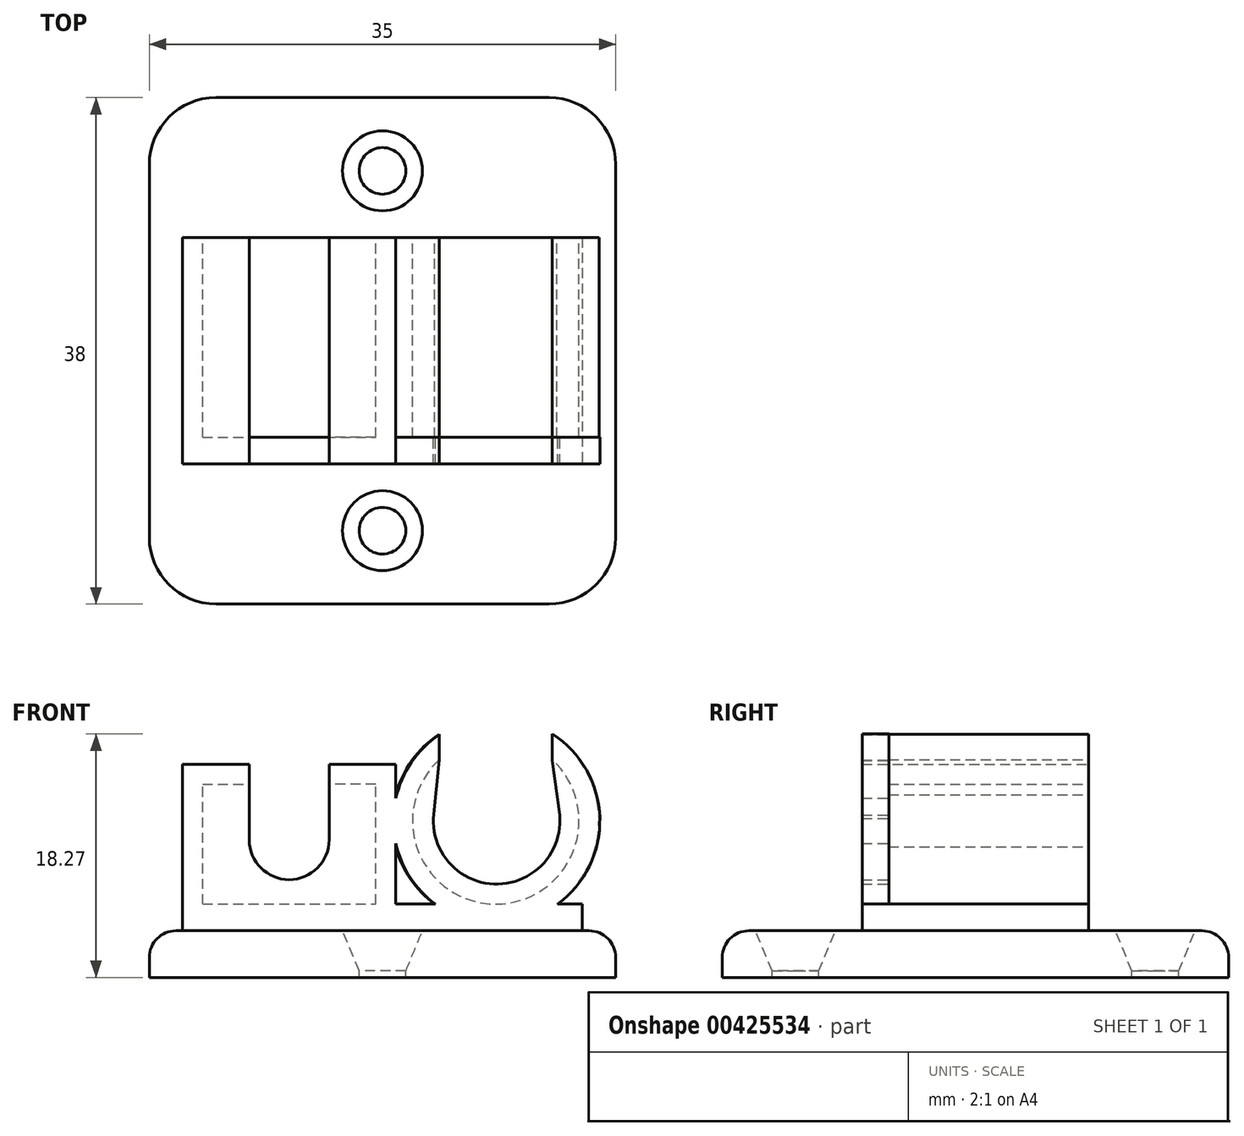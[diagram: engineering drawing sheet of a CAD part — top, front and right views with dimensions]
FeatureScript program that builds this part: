
annotation { "Feature Type Name" : "Feature", "Feature Type Description" : "" }
export const myFeature = defineFeature(function(context is Context, id is Id, definition is map)
    precondition{}
    {
        {
            var Q0;
            Q0=qCreatedBy(makeId("Top.planeOp"),FACE);
            var sketch = newSketch(context, id + "F0", { "sketchPlane" : qUnion([Q0])});
            skLineSegment(sketch, "E0.bottom", {"start": v(-17.5, 19) * mm, "end": v(17.5, 19) * mm});
            skLineSegment(sketch, "E0.top", {"start": v(-17.5, -19) * mm, "end": v(17.5, -19) * mm});
            skLineSegment(sketch, "E0.left", {"start": v(-17.5, 19) * mm, "end": v(-17.5, -19) * mm});
            skLineSegment(sketch, "E0.right", {"start": v(17.5, 19) * mm, "end": v(17.5, -19) * mm});
            skSolve(sketch);
        }
        {
            var Q0;
            Q0 = qSketchRegion(id + "F0", true);
            extrude(context, id + "F1", {"entities" : qUnion([Q0]), "depth" : 3.5 * mm});
        }
        {
            var Q0;
            Q0=makeQuery(id+"F1.opExtrude","CAP_FACE",FACE,{"disambiguationData":[OSD([sQuery(id+"F0.wireOp",EDGE,"E0.bottom"),sQuery(id+"F0.wireOp",EDGE,"E0.top"),sQuery(id+"F0.wireOp",EDGE,"E0.left"),sQuery(id+"F0.wireOp",EDGE,"E0.right")])],"isStart":false});
            var sketch = newSketch(context, id + "F2", { "sketchPlane" : qUnion([Q0])});
            skLineSegment(sketch, "E1.bottom", {"start": v(-15, 8.5) * mm, "end": v(15, 8.5) * mm});
            skLineSegment(sketch, "E1.top", {"start": v(-15, -8.5) * mm, "end": v(15, -8.5) * mm});
            skLineSegment(sketch, "E1.left", {"start": v(-15, 8.5) * mm, "end": v(-15, -8.5) * mm});
            skLineSegment(sketch, "E1.right", {"start": v(15, 8.5) * mm, "end": v(15, -8.5) * mm});
            skSolve(sketch);
        }
        {
            var Q0;
            Q0 = qSketchRegion(id + "F2", true);
            extrude(context, id + "F3", {"entities" : qUnion([Q0]), "operationType" : NewBodyOperationType.ADD, "depth" : 2 * mm});
        }
        {
            var Q0;
            Q0=makeQuery(id+"F3.opExtrude","SWEPT_FACE",FACE,{"disambiguationData":[OSD([sQuery(id+"F2.wireOp",EDGE,"E1.bottom")])]});
            var sketch = newSketch(context, id + "F4", { "sketchPlane" : qUnion([Q0])});
            skLineSegment(sketch, "E2.0", {"start": v(-12.75, 16.33) * mm, "end": v(-12.75, 18.23) * mm});
            skLineSegment(sketch, "E3.0", {"start": v(-4.25, 16.33) * mm, "end": v(-4.25, 18.23) * mm});
            skArc(sketch, "E4", {"start": v(-12.75, 16.33) * mm, "mid": v(-8.5, 5.5) * mm, "end": v(-4.25, 16.33) * mm});
            skArc(sketch, "E5", {"start": v(-12.75, 18.23) * mm, "mid": v(-8.5, 4) * mm, "end": v(-4.25, 18.23) * mm});
            skLineSegment(sketch, "E6", {"start": v(15, 5.5) * mm, "end": v(15, 16) * mm});
            skLineSegment(sketch, "E7.0", {"start": v(-1, 5.5) * mm, "end": v(-1, 16) * mm});
            skLineSegment(sketch, "E8", {"start": v(15, 16) * mm, "end": v(10, 16) * mm});
            skLineSegment(sketch, "E9", {"start": v(10, 16) * mm, "end": v(10, 14.5) * mm});
            skLineSegment(sketch, "E10", {"start": v(-1, 16) * mm, "end": v(4, 16) * mm});
            skLineSegment(sketch, "E11", {"start": v(4, 16) * mm, "end": v(4, 14.5) * mm});
            skLineSegment(sketch, "E12.0", {"start": v(13.5, 5.5) * mm, "end": v(13.5, 14.5) * mm});
            skLineSegment(sketch, "E13.0", {"start": v(0.5, 5.5) * mm, "end": v(0.5, 14.5) * mm});
            skLineSegment(sketch, "E14.0", {"start": v(0.5, 14.5) * mm, "end": v(4, 14.5) * mm});
            skLineSegment(sketch, "E15.0", {"start": v(13.5, 14.5) * mm, "end": v(10, 14.5) * mm});
            skLineSegment(sketch, "E16", {"start": v(-1, 5.5) * mm, "end": v(0.5, 5.5) * mm});
            skLineSegment(sketch, "E17", {"start": v(13.5, 5.5) * mm, "end": v(15, 5.5) * mm});
            skSolve(sketch);
        }
        {
            var Q0;
            Q0 = qSketchRegion(id + "F4", true);
            extrude(context, id + "F5", {"entities" : qUnion([Q0]), "operationType" : NewBodyOperationType.ADD, "oppositeDirection" : true, "depth" : 15 * mm});
        }
        {
            var Q0;
            Q0=makeQuery(id+"F1.opExtrude","CAP_FACE",FACE,{"disambiguationData":[OSD([sQuery(id+"F0.wireOp",EDGE,"E0.bottom"),sQuery(id+"F0.wireOp",EDGE,"E0.top"),sQuery(id+"F0.wireOp",EDGE,"E0.left"),sQuery(id+"F0.wireOp",EDGE,"E0.right")])],"isStart":false});
            var sketch = newSketch(context, id + "F6", { "sketchPlane" : qUnion([Q0])});
            skPoint(sketch, "E18", {"position": v(0, 13.5) * mm});
            skPoint(sketch, "E19", {"position": v(0, -13.5) * mm});
            skPoint(sketch, "E19.positionSnap0", {"position": v(0, 8.5) * mm});
            skSolve(sketch);
        }
        {
            var Q0;
            Q0=sQuery(id+"F6.wireOp",VERTEX,"E18");
            var Q1;
            Q1=sQuery(id+"F6.wireOp",VERTEX,"E19");
            var Q2;
            Q2=makeQuery(id+"F1.opExtrude","SWEPT_BODY",BODY,{"disambiguationData":[OSD([sQuery(id+"F0.wireOp",EDGE,"E0.bottom"),sQuery(id+"F0.wireOp",EDGE,"E0.top"),sQuery(id+"F0.wireOp",EDGE,"E0.left"),sQuery(id+"F0.wireOp",EDGE,"E0.right")])]});
            hole(context, id + "F7", {"style" : HoleStyle.C_SINK, "endStyle" : HoleEndStyle.BLIND, "holeDiameter" : 3.5 * mm, "cSinkDiameter" : 6 * mm, "cSinkAngle" : 45 * degree, "holeDepth" : 10 * mm, "isTappedThrough" : true, "tappedDepth" : 12 * mm, "tapClearance" : 3, "startFromSketch" : true, "locations" : qUnion([Q0, Q1]), "scope" : qUnion([Q2])});
        }
        {
            var Q0;
            Q0=makeQuery(id+"F5.opExtrude","CAP_FACE",FACE,{"disambiguationData":[OSD([sQuery(id+"F4.wireOp",EDGE,"E6"),sQuery(id+"F4.wireOp",EDGE,"E8"),sQuery(id+"F4.wireOp",EDGE,"E9"),sQuery(id+"F4.wireOp",EDGE,"E12.0"),sQuery(id+"F4.wireOp",EDGE,"E15.0"),sQuery(id+"F4.wireOp",EDGE,"E17")])],"isStart":false});
            var sketch = newSketch(context, id + "F8", { "sketchPlane" : qUnion([Q0])});
            skLineSegment(sketch, "E20.bottom", {"start": v(-15, 16) * mm, "end": v(-10, 16) * mm});
            skLineSegment(sketch, "E20.top", {"start": v(-15, 5.45) * mm, "end": v(1, 5.45) * mm});
            skLineSegment(sketch, "E20.left", {"start": v(-15, 16) * mm, "end": v(-15, 5.45) * mm});
            skLineSegment(sketch, "E20.right", {"start": v(1, 16) * mm, "end": v(1, 5.45) * mm});
            skLineSegment(sketch, "E21", {"start": v(-10, 16) * mm, "end": v(-10, 10.33) * mm});
            skLineSegment(sketch, "E22", {"start": v(-4, 16) * mm, "end": v(-4, 10.33) * mm});
            skLineSegment(sketch, "E23", {"start": v(-10, 10.33) * mm, "end": v(-10, 10.33) * mm});
            skArc(sketch, "E24", {"start": v(-10, 10.33) * mm, "mid": v(-7, 7.33) * mm, "end": v(-4, 10.33) * mm});
            skLineSegment(sketch, "E25", {"start": v(-4, 16) * mm, "end": v(1, 16) * mm});
            skLineSegment(sketch, "E26", {"start": v(12.75, 18.27) * mm, "end": v(12.75, 16.29) * mm});
            skLineSegment(sketch, "E27", {"start": v(12.75, 16.29) * mm, "end": v(13.3, 12.18) * mm});
            skLineSegment(sketch, "E28", {"start": v(4.26, 18.2) * mm, "end": v(4.26, 16.31) * mm});
            skLineSegment(sketch, "E29", {"start": v(4.26, 16.31) * mm, "end": v(3.82, 11.93) * mm});
            skArc(sketch, "E30", {"start": v(4.26, 18.2) * mm, "mid": v(8.63, 4) * mm, "end": v(12.75, 18.27) * mm});
            skLineSegment(sketch, "E31", {"start": v(3.82, 11.93) * mm, "end": v(3.82, 11.93) * mm});
            skArc(sketch, "E32", {"start": v(3.82, 11.93) * mm, "mid": v(8.69, 7) * mm, "end": v(13.3, 12.18) * mm});
            skSolve(sketch);
        }
        {
            var Q0;
            Q0 = qSketchRegion(id + "F8", true);
            extrude(context, id + "F9", {"entities" : qUnion([Q0]), "operationType" : NewBodyOperationType.ADD, "depth" : 2 * mm});
        }
        {
            var Q0;
            Q0=makeQuery(id+"F1.opExtrude","SWEPT_EDGE",EDGE,{"disambiguationData":[OSD([sQuery(id+"F0.wireOp",EDGE,"E0.bottom"),sQuery(id+"F0.wireOp",EDGE,"E0.left")])]});
            var Q1;
            Q1=makeQuery(id+"F1.opExtrude","SWEPT_EDGE",EDGE,{"disambiguationData":[OSD([sQuery(id+"F0.wireOp",EDGE,"E0.bottom"),sQuery(id+"F0.wireOp",EDGE,"E0.right")])]});
            var Q2;
            Q2=makeQuery(id+"F1.opExtrude","SWEPT_EDGE",EDGE,{"disambiguationData":[OSD([sQuery(id+"F0.wireOp",EDGE,"E0.top"),sQuery(id+"F0.wireOp",EDGE,"E0.left")])]});
            var Q3;
            Q3=makeQuery(id+"F1.opExtrude","SWEPT_EDGE",EDGE,{"disambiguationData":[OSD([sQuery(id+"F0.wireOp",EDGE,"E0.top"),sQuery(id+"F0.wireOp",EDGE,"E0.right")])]});
            fillet(context, id + "F10", {"entities" : qUnion([Q0, Q1, Q2, Q3]), "radius" : 5 * mm, "tangentPropagation" : true, "allowEdgeOverflow" : false});
        }
        {
            var Q0;
            Q0=makeQuery(id+"F1.opExtrude","CAP_EDGE",EDGE,{"disambiguationData":[OSD([sQuery(id+"F0.wireOp",EDGE,"E0.top")])],"isStart":false});
            fillet(context, id + "F11", {"entities" : qUnion([Q0]), "radius" : 2 * mm, "tangentPropagation" : true, "allowEdgeOverflow" : false});
        }
    });
